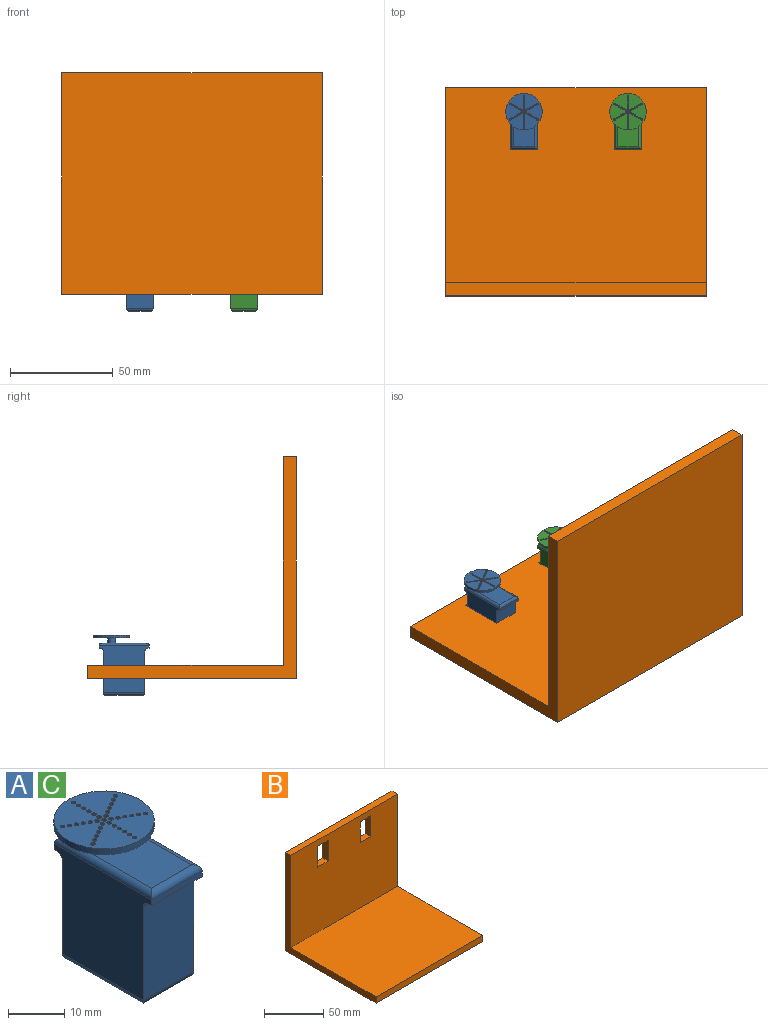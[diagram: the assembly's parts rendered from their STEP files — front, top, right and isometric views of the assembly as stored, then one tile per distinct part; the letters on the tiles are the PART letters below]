
ASSEMBLY  parts=3 mates=2
PART A: 68 faces, bbox 17.8x27.1x29.2 mm
  f0: plane 20.32x12.7mm, normal (0,-1,0), area 258.1mm2, adj f2,f3,f15,f20
  f1: plane 20.32x12.7mm, normal (0,1,0), area 258.1mm2, adj f2,f3,f16,f17
  f2: plane 24.38x22.86mm, normal (-1,0,0), area 470.4mm2, adj f0,f1,f7,f8,f9,f10,f12,f15
  f3: plane 24.38x22.86mm, normal (1,0,0), area 470.4mm2, adj f0,f1,f7,f8,f9,f10,f13,f15
  f4: plane 21.84x10.16mm, normal (0,0,1), area 210.5mm2, adj f6,f11,f12,f13,f14
  f5: plane 17.78x10.16mm, normal (0,0,-1), area 180.6mm2, adj f17,f18,f19,f20
  f6: cylinder r=1.91mm len=3.81mm, axis (0,0,-1), area 30.4mm2, adj f4,f23
  f7: plane 12.7x1.27mm, normal (0,1,0), area 16.1mm2, adj f2,f3,f8,f11
  f8: plane 12.7x0.76mm, normal (0,0,-1), area 9.7mm2, adj f2,f3,f7,f16
  f9: plane 12.7x1.27mm, normal (0,-1,0), area 16.1mm2, adj f2,f3,f10,f14
  f10: plane 12.7x0.76mm, normal (0,0,-1), area 9.7mm2, adj f2,f3,f9,f15
  f11: cylinder r=1.27mm len=12.7mm, axis (-1,0,0), area 23.5mm2, adj f4,f7,f12,f13
  f12: cylinder r=1.27mm len=24.38mm, axis (0,1,0), area 46.8mm2, adj f2,f4,f11,f14
  f13: cylinder r=1.27mm len=24.38mm, axis (0,-1,0), area 46.8mm2, adj f3,f4,f11,f14
  f14: cylinder r=1.27mm len=12.7mm, axis (1,0,0), area 23.5mm2, adj f4,f9,f12,f13
  f15: cylinder r=1.27mm len=12.7mm, axis (-1,0,0), area 25.3mm2, adj f0,f2,f3,f10
  f16: cylinder r=1.27mm len=12.7mm, axis (1,0,0), area 25.3mm2, adj f1,f2,f3,f8
  f17: cylinder r=1.27mm len=12.7mm, axis (-1,0,0), area 23.5mm2, adj f1,f5,f18,f19
  f18: cylinder r=1.27mm len=20.32mm, axis (0,-1,0), area 38.7mm2, adj f2,f5,f17,f20
  f19: cylinder r=1.27mm len=20.32mm, axis (0,1,0), area 38.7mm2, adj f3,f5,f17,f20
  f20: cylinder r=1.27mm len=12.7mm, axis (1,0,0), area 23.5mm2, adj f0,f5,f18,f19
  f21: cylinder r=8.89mm len=17.78mm, axis (0,0,-1), area 70.9mm2, adj f22,f23
  f22: plane 17.78x17.78mm, normal (0,0,1), area 231.4mm2, adj f21,f24,f25,f26,f27,f28,f29,f30
  f23: plane 17.78x17.78mm, normal (0,0,-1), area 223.2mm2, adj f6,f21,f24,f25,f26,f27,f28,f29
  f24: cylinder r=0.38mm len=1.27mm, axis (0,0,1), area 3mm2, adj f22,f23
  f25: cylinder r=0.38mm len=1.27mm, axis (0,0,1), area 3mm2, adj f22,f23
  f26: cylinder r=0.38mm len=1.27mm, axis (0,0,1), area 3mm2, adj f22,f23
  f27: cylinder r=0.38mm len=1.27mm, axis (0,0,1), area 3mm2, adj f22,f23
  f28: cylinder r=0.38mm len=1.27mm, axis (0,0,1), area 3mm2, adj f22,f23
  f29: cylinder r=0.38mm len=1.27mm, axis (0,0,1), area 3mm2, adj f22,f23
  f30: cylinder r=0.38mm len=1.27mm, axis (0,0,1), area 3mm2, adj f22,f23
  f31: cylinder r=0.38mm len=1.27mm, axis (0,0,1), area 3mm2, adj f22,f23
  f32: cylinder r=0.38mm len=1.27mm, axis (0,0,1), area 3mm2, adj f22,f23
  f33: cylinder r=0.38mm len=1.27mm, axis (0,0,1), area 3mm2, adj f22,f23
  f34: cylinder r=0.38mm len=1.27mm, axis (0,0,1), area 3mm2, adj f22,f23
  f35: cylinder r=0.38mm len=1.27mm, axis (0,0,1), area 3mm2, adj f22,f23
  f36: cylinder r=0.38mm len=1.27mm, axis (0,0,1), area 3mm2, adj f22,f23
  f37: cylinder r=0.38mm len=1.27mm, axis (0,0,1), area 3mm2, adj f22,f23
  f38: cylinder r=0.38mm len=1.27mm, axis (0,0,1), area 3mm2, adj f22,f23
  f39: cylinder r=0.38mm len=1.27mm, axis (0,0,1), area 3mm2, adj f22,f23
  f40: cylinder r=0.38mm len=1.27mm, axis (0,0,1), area 3mm2, adj f22,f23
  f41: cylinder r=0.38mm len=1.27mm, axis (0,0,1), area 3mm2, adj f22,f23
  f42: cylinder r=0.38mm len=1.27mm, axis (0,0,1), area 3mm2, adj f22,f23
  f43: cylinder r=0.38mm len=1.27mm, axis (0,0,1), area 3mm2, adj f22,f23
  f44: cylinder r=0.38mm len=1.27mm, axis (0,0,1), area 3mm2, adj f22,f23
  f45: cylinder r=0.38mm len=1.27mm, axis (0,0,1), area 3mm2, adj f22,f23
  f46: cylinder r=0.38mm len=1.27mm, axis (0,0,1), area 3mm2, adj f22,f23
  f47: cylinder r=0.38mm len=1.27mm, axis (0,0,1), area 3mm2, adj f22,f23
  f48: cylinder r=0.38mm len=1.27mm, axis (0,0,1), area 3mm2, adj f22,f23
  f49: cylinder r=0.38mm len=1.27mm, axis (0,0,1), area 3mm2, adj f22,f23
  f50: cylinder r=0.38mm len=1.27mm, axis (0,0,1), area 3mm2, adj f22,f23
  f51: cylinder r=0.38mm len=1.27mm, axis (0,0,1), area 3mm2, adj f22,f23
  f52: cylinder r=0.38mm len=1.27mm, axis (0,0,1), area 3mm2, adj f22,f23
  f53: cylinder r=0.38mm len=1.27mm, axis (0,0,1), area 3mm2, adj f22,f23
  f54: cylinder r=0.38mm len=1.27mm, axis (0,0,1), area 3mm2, adj f22,f55
  f55: plane 0.76x0.76mm, normal (0,0,1), area 0.5mm2, adj f54
  f56: cylinder r=0.38mm len=1.27mm, axis (0,0,1), area 3mm2, adj f22,f57
  f57: plane 0.76x0.76mm, normal (0,0,1), area 0.5mm2, adj f56
  f58: cylinder r=0.38mm len=1.27mm, axis (0,0,1), area 3mm2, adj f22,f59
  f59: plane 0.76x0.76mm, normal (0,0,1), area 0.5mm2, adj f58
  f60: cylinder r=0.38mm len=1.27mm, axis (0,0,1), area 3mm2, adj f22,f61
  f61: plane 0.76x0.76mm, normal (0,0,1), area 0.5mm2, adj f60
  f62: cylinder r=0.38mm len=1.27mm, axis (0,0,1), area 3mm2, adj f22,f63
  f63: plane 0.76x0.76mm, normal (0,0,1), area 0.5mm2, adj f62
  f64: cylinder r=0.38mm len=1.27mm, axis (0,0,1), area 3mm2, adj f22,f65
  f65: plane 0.76x0.76mm, normal (0,0,1), area 0.5mm2, adj f64
  f66: cylinder r=0.38mm len=1.27mm, axis (0,0,1), area 3mm2, adj f22,f67
  f67: plane 0.76x0.76mm, normal (0,0,1), area 0.5mm2, adj f66
PART B: 16 faces, bbox 127x108x101.6 mm
  f0: plane 127x95.25mm, normal (0,-1,0), area 11548.4mm2, adj f2,f4,f5,f7,f8,f9,f10,f11
  f1: plane 127x101.6mm, normal (0,1,0), area 12354.8mm2, adj f2,f4,f6,f7,f8,f9,f10,f11
  f2: plane 107.95x101.6mm, normal (-1,0,0), area 1290.3mm2, adj f0,f1,f3,f5,f6,f7
  f3: plane 127x6.35mm, normal (0,-1,0), area 806.5mm2, adj f2,f4,f5,f6
  f4: plane 107.95x101.6mm, normal (1,0,0), area 1290.3mm2, adj f0,f1,f3,f5,f6,f7
  f5: plane 127x101.6mm, normal (0,0,1), area 12903.2mm2, adj f0,f2,f3,f4
  f6: plane 127x107.95mm, normal (0,0,-1), area 13709.6mm2, adj f1,f2,f3,f4
  f7: plane 127x6.35mm, normal (0,0,1), area 806.5mm2, adj f0,f1,f2,f4
  f8: plane 21.59x6.35mm, normal (-1,0,0), area 137.1mm2, adj f0,f1,f9,f11
  f9: plane 12.7x6.35mm, normal (0,0,-1), area 80.6mm2, adj f0,f1,f8,f10
  f10: plane 21.59x6.35mm, normal (1,0,0), area 137.1mm2, adj f0,f1,f9,f11
  f11: plane 12.7x6.35mm, normal (0,0,1), area 80.6mm2, adj f0,f1,f8,f10
  f12: plane 12.7x6.35mm, normal (0,0,-1), area 80.6mm2, adj f0,f1,f13,f15
  f13: plane 21.59x6.35mm, normal (1,0,0), area 137.1mm2, adj f0,f1,f12,f14
  f14: plane 12.7x6.35mm, normal (0,0,1), area 80.6mm2, adj f0,f1,f13,f15
  f15: plane 21.59x6.35mm, normal (-1,0,0), area 137.1mm2, adj f0,f1,f12,f14
PART C: same geometry as A
PLACE A t=(-50.99,29.96,32.65)mm
PLACE B rot(axis=(-1,0,0),90deg) t=(-25.65,-53.9,98.06)mm
PLACE C t=(-0.32,29.96,32.65)mm
MATE parallel B.f11 <-> C.f0  axis (0,1,0) through (-0.32,19.8,44.08)mm
MATE parallel A.f0 <-> B.f14  axis (0,-1,0) through (-50.99,19.8,44.08)mm
